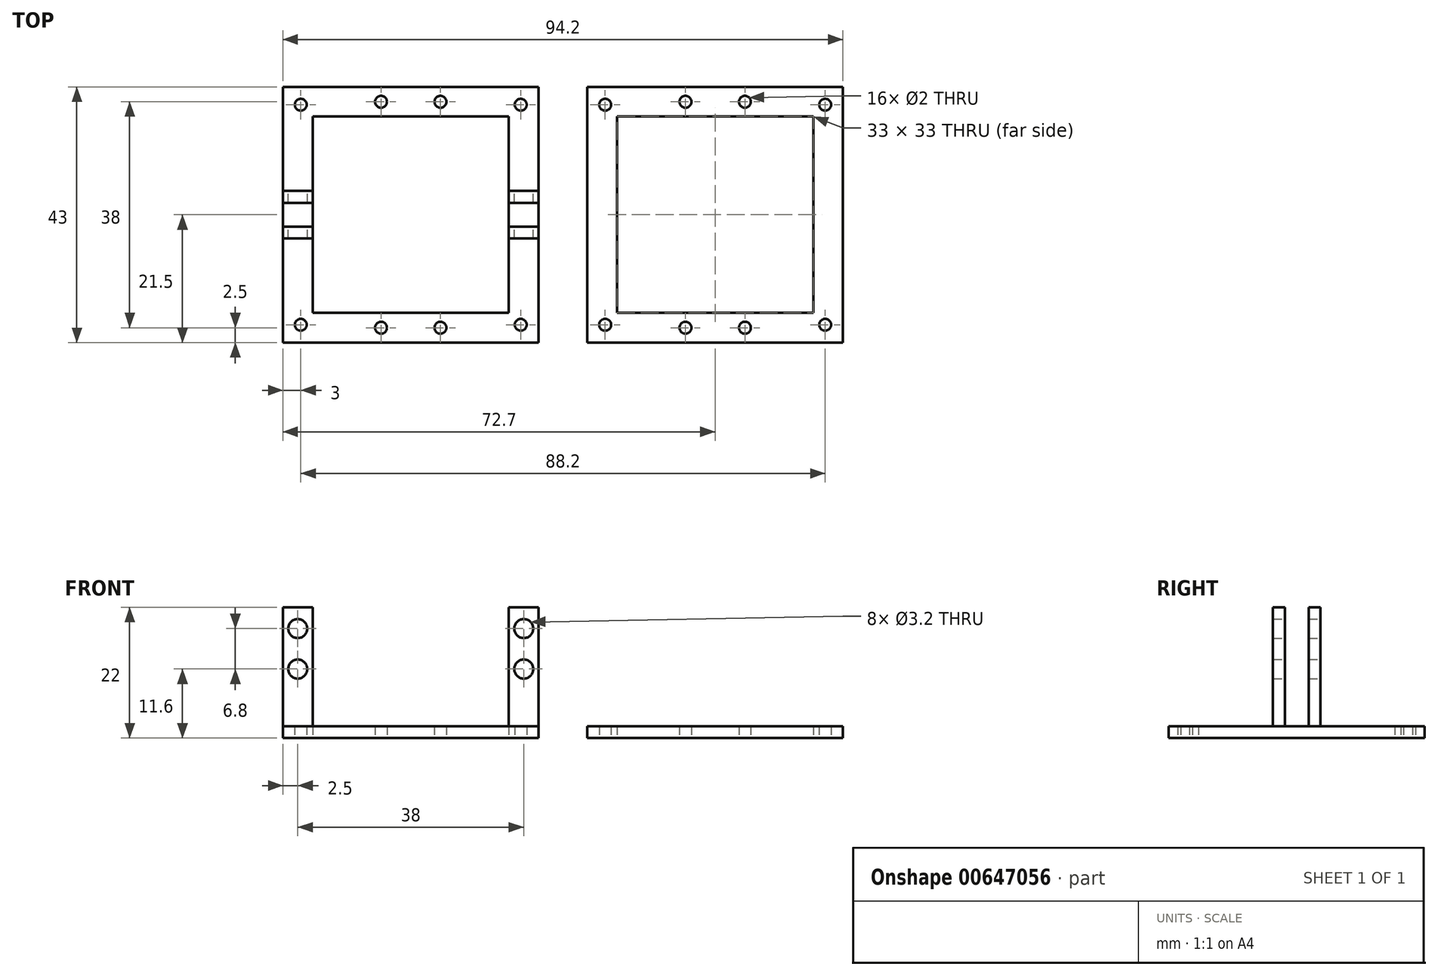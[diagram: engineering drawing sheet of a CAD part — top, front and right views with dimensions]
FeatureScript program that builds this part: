
annotation { "Feature Type Name" : "Feature", "Feature Type Description" : "" }
export const myFeature = defineFeature(function(context is Context, id is Id, definition is map)
    precondition{}
    {
        {
            var Q0;
            Q0=qCreatedBy(makeId("Top.planeOp"),FACE);
            var sketch = newSketch(context, id + "F0", { "sketchPlane" : qUnion([Q0])});
            skLineSegment(sketch, "E0.bottom", {"start": v(-21.5, 21.5) * mm, "end": v(21.5, 21.5) * mm});
            skLineSegment(sketch, "E0.top", {"start": v(-21.5, -21.5) * mm, "end": v(21.5, -21.5) * mm});
            skLineSegment(sketch, "E0.left", {"start": v(-21.5, 21.5) * mm, "end": v(-21.5, -21.5) * mm});
            skLineSegment(sketch, "E0.right", {"start": v(21.5, 21.5) * mm, "end": v(21.5, -21.5) * mm});
            skPoint(sketch, "E0.middle", {"position": v(0, 0) * mm});
            skLineSegment(sketch, "E1.bottom", {"start": v(-16.5, 16.5) * mm, "end": v(16.5, 16.5) * mm});
            skLineSegment(sketch, "E1.top", {"start": v(-16.5, -16.5) * mm, "end": v(16.5, -16.5) * mm});
            skLineSegment(sketch, "E1.left", {"start": v(-16.5, 16.5) * mm, "end": v(-16.5, -16.5) * mm});
            skLineSegment(sketch, "E1.right", {"start": v(16.5, 16.5) * mm, "end": v(16.5, -16.5) * mm});
            skCircle(sketch, "E2", {"center": v(-18.5, 18.5) * mm, "radius": 1 * mm});
            skCircle(sketch, "E3.1.0", {"center": v(-18.5, -18.5) * mm, "radius": 1 * mm});
            skCircle(sketch, "E3.2.0", {"center": v(18.5, -18.5) * mm, "radius": 1 * mm});
            skCircle(sketch, "E3.3.0", {"center": v(18.5, 18.5) * mm, "radius": 1 * mm});
            skCircle(sketch, "E4.1.0", {"center": v(-5, -19) * mm, "radius": 1 * mm});
            skCircle(sketch, "E4.3.0", {"center": v(5, 19) * mm, "radius": 1 * mm});
            skCircle(sketch, "E5.1.0", {"center": v(5, -19) * mm, "radius": 1 * mm});
            skCircle(sketch, "E5.3.0", {"center": v(-5, 19) * mm, "radius": 1 * mm});
            skSolve(sketch);
        }
        {
            var Q0;
            Q0=makeQuery(id+"F0.imprint","IMPRINT",FACE,{"disambiguationData":[TD([[makeQuery(id+"F0.imprint","IMPRINT",EDGE,{"derivedFrom":sQuery(id+"F0.wireOp",EDGE,"E0.bottom")}),-1.0]])]});
            extrude(context, id + "F1", {"entities" : qUnion([Q0]), "depth" : 2 * mm, "offsetDistance" : 25 * mm});
        }
        {
            var Q0;
            Q0=makeQuery(id+"F1.opExtrude","SWEPT_BODY",BODY,{"disambiguationData":[OSD([sQuery(id+"F0.wireOp",EDGE,"E0.bottom"),sQuery(id+"F0.wireOp",EDGE,"E0.top"),sQuery(id+"F0.wireOp",EDGE,"E0.left"),sQuery(id+"F0.wireOp",EDGE,"E0.right"),sQuery(id+"F0.wireOp",EDGE,"E1.bottom"),sQuery(id+"F0.wireOp",EDGE,"E1.top"),sQuery(id+"F0.wireOp",EDGE,"E1.left"),sQuery(id+"F0.wireOp",EDGE,"E1.right"),sQuery(id+"F0.wireOp",EDGE,"E2"),sQuery(id+"F0.wireOp",EDGE,"E3.1.0"),sQuery(id+"F0.wireOp",EDGE,"E3.2.0"),sQuery(id+"F0.wireOp",EDGE,"E3.3.0")])]});
            transform(context, id + "F2", {"entities" : qUnion([Q0]), "transformType" : TransformType.TRANSLATION_3D, "dx" : 51.2 * mm, "dy" : -2.17E-16 * mm, "dz" : 0 * mm, "makeCopy" : true});
        }
        {
            var Q0;
            Q0=qCreatedBy(makeId("Right.planeOp"),FACE);
            var sketch = newSketch(context, id + "F3", { "sketchPlane" : qUnion([Q0])});
            skLineSegment(sketch, "E6.bottom", {"start": v(-4, 22) * mm, "end": v(4, 22) * mm});
            skLineSegment(sketch, "E6.top", {"start": v(-4, 2) * mm, "end": v(4, 2) * mm});
            skLineSegment(sketch, "E6.left", {"start": v(-4, 22) * mm, "end": v(-4, 2) * mm});
            skLineSegment(sketch, "E6.right", {"start": v(4, 22) * mm, "end": v(4, 2) * mm});
            skPoint(sketch, "E6.middle", {"position": v(0, 12) * mm});
            skLineSegment(sketch, "E7.bottom", {"start": v(-2, 22) * mm, "end": v(2, 22) * mm});
            skLineSegment(sketch, "E7.top", {"start": v(-2, 2) * mm, "end": v(2, 2) * mm});
            skLineSegment(sketch, "E7.left", {"start": v(-2, 22) * mm, "end": v(-2, 2) * mm});
            skLineSegment(sketch, "E7.right", {"start": v(2, 22) * mm, "end": v(2, 2) * mm});
            skSolve(sketch);
        }
        {
            var Q0;
            {var subQ0=sQuery(id+"F3.wireOp",EDGE,"E6.right");Q0=makeQuery(id+"F3.imprint","IMPRINT",FACE,{"disambiguationData":[TD([[makeQuery(id+"F3.imprint","IMPRINT",EDGE,{"derivedFrom":subQ0}),-1.0]])]});}
            var Q1;
            {var subQ0=sQuery(id+"F3.wireOp",EDGE,"E6.left");Q1=makeQuery(id+"F3.imprint","IMPRINT",FACE,{"disambiguationData":[TD([[makeQuery(id+"F3.imprint","IMPRINT",EDGE,{"derivedFrom":subQ0}),1.0]])]});}
            extrude(context, id + "F4", {"entities" : qUnion([Q0, Q1]), "operationType" : NewBodyOperationType.ADD, "endBound" : BoundingType.SYMMETRIC, "oppositeDirection" : true, "depth" : 43 * mm, "offsetDistance" : 25 * mm, "hasSecondDirection" : true, "secondDirectionOppositeDirection" : false, "secondDirectionDepth" : 25 * mm});
        }
        {
            var Q0;
            Q0=makeQuery(id+"F1.opExtrude","CAP_FACE",FACE,{"disambiguationData":[OSD([sQuery(id+"F0.wireOp",EDGE,"E0.bottom"),sQuery(id+"F0.wireOp",EDGE,"E0.top"),sQuery(id+"F0.wireOp",EDGE,"E0.left"),sQuery(id+"F0.wireOp",EDGE,"E0.right"),sQuery(id+"F0.wireOp",EDGE,"E1.bottom"),sQuery(id+"F0.wireOp",EDGE,"E1.top"),sQuery(id+"F0.wireOp",EDGE,"E1.left"),sQuery(id+"F0.wireOp",EDGE,"E1.right"),sQuery(id+"F0.wireOp",EDGE,"E2"),sQuery(id+"F0.wireOp",EDGE,"E3.1.0"),sQuery(id+"F0.wireOp",EDGE,"E3.2.0"),sQuery(id+"F0.wireOp",EDGE,"E3.3.0")])],"isStart":true});
            var sketch = newSketch(context, id + "F5", { "sketchPlane" : qUnion([Q0])});
            skLineSegment(sketch, "E8.bottom", {"start": v(-16.5, 16.5) * mm, "end": v(16.5, 16.5) * mm});
            skLineSegment(sketch, "E8.top", {"start": v(-16.5, -16.5) * mm, "end": v(16.5, -16.5) * mm});
            skLineSegment(sketch, "E8.left", {"start": v(-16.5, 16.5) * mm, "end": v(-16.5, -16.5) * mm});
            skLineSegment(sketch, "E8.right", {"start": v(16.5, 16.5) * mm, "end": v(16.5, -16.5) * mm});
            skPoint(sketch, "E8.middle", {"position": v(0, 0) * mm});
            skSolve(sketch);
        }
        {
            var Q0;
            Q0=makeQuery(id+"F5.imprint","IMPRINT",FACE,{"disambiguationData":[TD([[makeQuery(id+"F5.imprint","IMPRINT",EDGE,{"derivedFrom":sQuery(id+"F5.wireOp",EDGE,"E8.bottom")}),-1.0]])]});
            extrude(context, id + "F6", {"entities" : qUnion([Q0]), "operationType" : NewBodyOperationType.REMOVE, "oppositeDirection" : true, "depth" : 25 * mm, "offsetDistance" : 25 * mm});
        }
        {
            var Q0;
            {var subQ2=sQuery(id+"F3.wireOp",EDGE,"E6.right");var subQ5=sQuery(id+"F0.wireOp",EDGE,"E0.right");Q0=makeQuery(id+"F6.boolean.opBoolean","SPLIT",FACE,{"disambiguationData":[TD([makeQuery(id+"F1.opExtrude","SWEPT_FACE",FACE,{"disambiguationData":[OSD([subQ5])]})])],"derivedFrom":makeQuery(id+"F4.opExtrude","SWEPT_FACE",FACE,{"disambiguationData":[OSD([subQ2])]})});}
            var sketch = newSketch(context, id + "F7", { "sketchPlane" : qUnion([Q0])});
            skCircle(sketch, "E9", {"center": v(-19, 18.4) * mm, "radius": 1.6 * mm});
            skCircle(sketch, "E10.1.0.0", {"center": v(-19, 11.6) * mm, "radius": 1.6 * mm});
            skLineSegment(sketch, "E10.direction1", {"start": v(-19, 18.4) * mm, "end": v(-19, 11.6) * mm, "construction": true});
            skCircle(sketch, "E11.1.0.0", {"center": v(19, 18.4) * mm, "radius": 1.6 * mm});
            skCircle(sketch, "E11.1.0.1", {"center": v(19, 11.6) * mm, "radius": 1.6 * mm});
            skCircle(sketch, "E11.2.0.0", {"center": v(57, 18.4) * mm, "radius": 1.6 * mm});
            skCircle(sketch, "E11.2.0.1", {"center": v(57, 11.6) * mm, "radius": 1.6 * mm});
            skLineSegment(sketch, "E11.direction1", {"start": v(-19, 11.6) * mm, "end": v(19, 11.6) * mm, "construction": true});
            skSolve(sketch);
        }
        {
            var Q0;
            Q0=makeQuery(id+"F7.imprint","IMPRINT",FACE,{"disambiguationData":[TD([[makeQuery(id+"F7.imprint","IMPRINT",EDGE,{"derivedFrom":sQuery(id+"F7.wireOp",EDGE,"E9")}),1.0]])]});
            var Q1;
            Q1=makeQuery(id+"F7.imprint","IMPRINT",FACE,{"disambiguationData":[TD([[makeQuery(id+"F7.imprint","IMPRINT",EDGE,{"derivedFrom":sQuery(id+"F7.wireOp",EDGE,"E10.1.0.0")}),1.0]])]});
            var Q2;
            Q2=makeQuery(id+"F7.imprint","IMPRINT",FACE,{"disambiguationData":[TD([[makeQuery(id+"F7.imprint","IMPRINT",EDGE,{"derivedFrom":sQuery(id+"F7.wireOp",EDGE,"E11.1.0.0")}),1.0]])]});
            var Q3;
            Q3=makeQuery(id+"F7.imprint","IMPRINT",FACE,{"disambiguationData":[TD([[makeQuery(id+"F7.imprint","IMPRINT",EDGE,{"derivedFrom":sQuery(id+"F7.wireOp",EDGE,"E11.1.0.1")}),1.0]])]});
            extrude(context, id + "F8", {"entities" : qUnion([Q0, Q1, Q2, Q3]), "operationType" : NewBodyOperationType.REMOVE, "oppositeDirection" : true, "depth" : 25 * mm, "offsetDistance" : 25 * mm});
        }
    });
